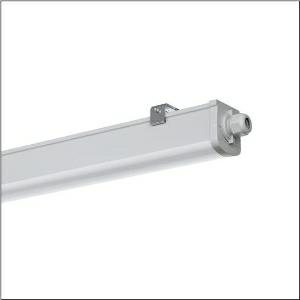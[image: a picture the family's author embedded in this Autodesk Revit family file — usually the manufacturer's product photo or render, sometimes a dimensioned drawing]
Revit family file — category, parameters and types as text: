
# Revit family: monsun_r__31_51fa207d420b_180d
name_source: partatom
category: Lighting Fixtures
units: mm (PartAtom-declared; Revit-internal decimal feet)

## family parameters
Cut with Voids When Loaded = No
Host = Face
Light Source = No
Part Type = Normal
Room Calculation Point = No
Round Connector Dimension = Use Diameter
Shared = No

## types (1)
- Monsun® 31 (1 x LED, 2300 lm, 19 W, 4000K)
    Apparent Load = 19 VA
    CIE Flux Codes = 42 72 91 92 100
    Color Rendering = 80
    Color Temperature = 4000K
    Default Elevation = 1800 mm
    Description = Monsun® 31, damp-proof luminaire, primary optical cover: diffuser, of PC, frosted, light emission: direct distribution, primary light characteristic: symmetric, installation type: surface-mounted, LED, rated luminous flux: 2.300lm, luminous efficacy: 121lm/W, light colour: 840, colour temperature: 4000K, control gear: ON/OFF, with terminal, 3+1-pole, max. 2.5mm², through-wiring: 3x 2.5mm² + 1x 1.5mm², mains connection: 220..240V, AC, 50/60Hz, rated input power: 19W, housing, luminaire housing, of PC, light grey (RAL 7035), length: 558mm, width: 68mm, height: 76mm, protection rating (complete): IP66, insulation class (complete): insulation class II (safety insulation), certification: CE, ENEC, UKCA, protection symbol: D, impact resistance: IK08, permissible operating ambient temperature: -20..+40°C, corresponds to IFS (International Featured Standards) requirements for safety and quality in the food industry, contact your sales advisor before using the luminaires in applications with unclear chemical exposure, large temperature fluctuations or condensation-forming humidity, packaging unit: 1 piece
    Height = 77 mm
    Lamp = 1 x LED
    Lamp Light Flux = 2300 lm
    Lamp Power = 19 W
    Lamp count = 1
    Length = 618 mm
    Luminous efficacy = 121 lm/W
    Manufacturer = Siteco
    ModVariant = No
    Model = 51FA207D420B
    Mounting Place = Ceiling
    Mounting Type = Surface mounted
    Number of Poles = 1
    OnlyDefault = Yes
    Power Factor = 1
    Product Name = Monsun® 31
    Product group = damp-proof luminaire
    ProductGroupID = 301
    Protection Class = Protection class II
    Protection Degree = IP 66
    RLX_Detail_Level = 1
    RLX_Emergency_Light_Flux = 0 lm
    RLX_Emergency_Type = 0
    RLX_Emergency_Type_DB = No
    RlxData = <blob elided: 32917 chars, md5=f44cc29f>
    Socket = socket
    Standby Power = 0 W
    System Light Flux = 2300 lm
    System Power = 19 W
    Type Comments = Product without accessories
    Type Image = l_1006174.jpg
    URL = http://relux.com
    VarID = ---
    Voltage = 0 V
    Weight = 0.00 kg
    Width = 69 mm

## geometry (parser evidence)
native form markers: Blend x4, Sweep x13
no freeform markers — native parametric forms only
